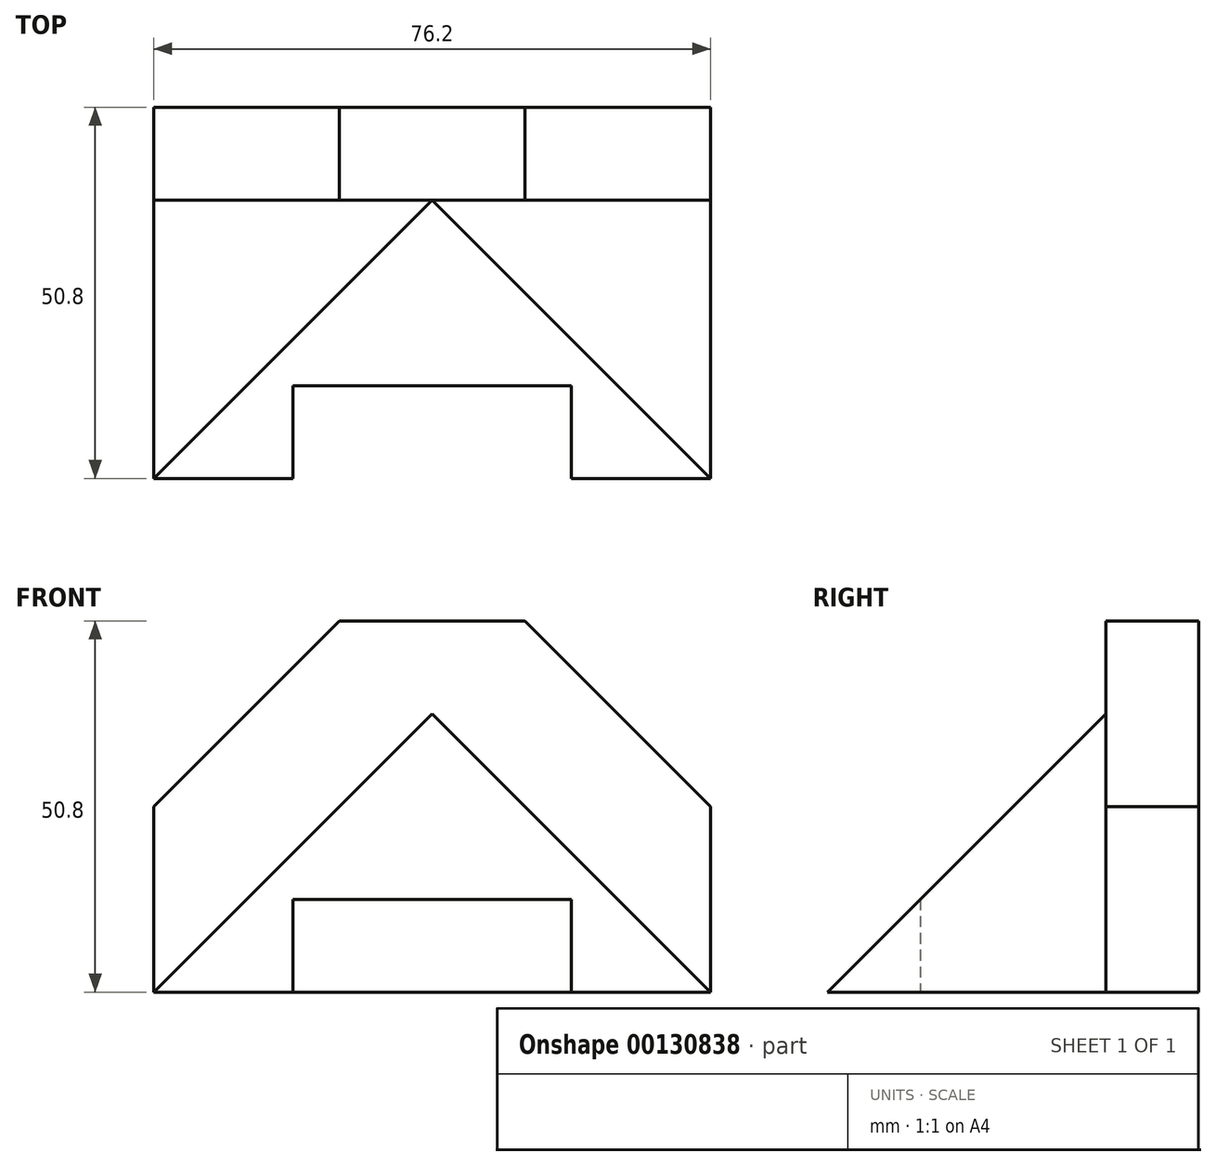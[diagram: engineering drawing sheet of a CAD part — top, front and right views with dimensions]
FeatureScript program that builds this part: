
annotation { "Feature Type Name" : "Feature", "Feature Type Description" : "" }
export const myFeature = defineFeature(function(context is Context, id is Id, definition is map)
    precondition{}
    {
        {
            var Q0;
            Q0=qCreatedBy(makeId("Front.planeOp"),FACE);
            var sketch = newSketch(context, id + "F0", { "sketchPlane" : qUnion([Q0])});
            skLineSegment(sketch, "E0", {"start": v(0, 0) * mm, "end": v(0, 25.4) * mm});
            skLineSegment(sketch, "E1", {"start": v(0, 25.4) * mm, "end": v(25.4, 50.8) * mm});
            skLineSegment(sketch, "E2", {"start": v(25.4, 50.8) * mm, "end": v(50.8, 50.8) * mm});
            skLineSegment(sketch, "E3", {"start": v(50.8, 50.8) * mm, "end": v(76.2, 25.4) * mm});
            skLineSegment(sketch, "E4", {"start": v(76.2, 25.4) * mm, "end": v(76.2, 0) * mm});
            skLineSegment(sketch, "E5", {"start": v(76.2, 0) * mm, "end": v(0, 0) * mm});
            skSolve(sketch);
        }
        {
            var Q0;
            Q0 = qSketchRegion(id + "F0", true);
            extrude(context, id + "F1", {"entities" : qUnion([Q0]), "oppositeDirection" : true, "depth" : 12.7 * mm});
        }
        {
            var Q0;
            Q0=qCreatedBy(makeId("Front.planeOp"),FACE);
            var sketch = newSketch(context, id + "F2", { "sketchPlane" : qUnion([Q0])});
            skLineSegment(sketch, "E6", {"start": v(0, 0) * mm, "end": v(0, 38.1) * mm});
            skLineSegment(sketch, "E7", {"start": v(0, 38.1) * mm, "end": v(76.2, 38.1) * mm});
            skLineSegment(sketch, "E8", {"start": v(76.2, 38.1) * mm, "end": v(76.2, 0) * mm});
            skLineSegment(sketch, "E9", {"start": v(76.2, 0) * mm, "end": v(0, 0) * mm});
            skSolve(sketch);
        }
        {
            var Q0;
            Q0 = qSketchRegion(id + "F2", true);
            extrude(context, id + "F3", {"entities" : qUnion([Q0]), "operationType" : NewBodyOperationType.ADD, "depth" : 38.1 * mm});
        }
        {
            var Q0;
            Q0=makeQuery(id+"F3.opExtrude","CAP_FACE",FACE,{"disambiguationData":[OSD([sQuery(id+"F2.wireOp",EDGE,"E6"),sQuery(id+"F2.wireOp",EDGE,"E7"),sQuery(id+"F2.wireOp",EDGE,"E8"),sQuery(id+"F2.wireOp",EDGE,"E9")])],"isStart":false});
            var sketch = newSketch(context, id + "F4", { "sketchPlane" : qUnion([Q0])});
            skLineSegment(sketch, "E10", {"start": v(0, 0) * mm, "end": v(38.1, 38.1) * mm});
            skLineSegment(sketch, "E11", {"start": v(38.1, 38.1) * mm, "end": v(76.2, 0) * mm});
            skLineSegment(sketch, "E12", {"start": v(0, 0) * mm, "end": v(0, 38.1) * mm});
            skLineSegment(sketch, "E13", {"start": v(0, 38.1) * mm, "end": v(38.1, 38.1) * mm});
            skLineSegment(sketch, "E14", {"start": v(38.1, 38.1) * mm, "end": v(76.2, 38.1) * mm});
            skLineSegment(sketch, "E15", {"start": v(76.2, 38.1) * mm, "end": v(76.2, 0) * mm});
            skSolve(sketch);
        }
        {
            var Q0;
            Q0 = qSketchRegion(id + "F4", true);
            extrude(context, id + "F5", {"entities" : qUnion([Q0]), "operationType" : NewBodyOperationType.REMOVE, "oppositeDirection" : true, "depth" : 38.1 * mm});
        }
        {
            var Q0;
            Q0=qCreatedBy(makeId("Right.planeOp"),FACE);
            var sketch = newSketch(context, id + "F6", { "sketchPlane" : qUnion([Q0])});
            skLineSegment(sketch, "E16.0", {"start": v(0, 38.1) * mm, "end": v(-38.1, 38.1) * mm});
            skLineSegment(sketch, "E17.0", {"start": v(-38.1, 0) * mm, "end": v(-38.1, 38.1) * mm});
            skLineSegment(sketch, "E18", {"start": v(0, 38.1) * mm, "end": v(-38.1, 0) * mm});
            skSolve(sketch);
        }
        {
            var Q0;
            Q0 = qSketchRegion(id + "F6", true);
            extrude(context, id + "F7", {"entities" : qUnion([Q0]), "operationType" : NewBodyOperationType.REMOVE, "endBound" : BoundingType.THROUGH_ALL, "depth" : 25.4 * mm});
        }
        {
            var Q0;
            Q0=qCreatedBy(makeId("Top.planeOp"),FACE);
            var sketch = newSketch(context, id + "F8", { "sketchPlane" : qUnion([Q0])});
            skLineSegment(sketch, "E19.0", {"start": v(57.15, -38.1) * mm, "end": v(19.05, -38.1) * mm});
            skLineSegment(sketch, "E20", {"start": v(19.05, -38.1) * mm, "end": v(19.05, -25.4) * mm});
            skLineSegment(sketch, "E21", {"start": v(19.05, -25.4) * mm, "end": v(57.15, -25.4) * mm});
            skLineSegment(sketch, "E22", {"start": v(57.15, -25.4) * mm, "end": v(57.15, -38.1) * mm});
            skPoint(sketch, "E23.orphan", {"position": v(0, -38.1) * mm});
            skPoint(sketch, "E24.orphan", {"position": v(76.2, -38.1) * mm});
            skSolve(sketch);
        }
        {
            var Q0;
            Q0 = qSketchRegion(id + "F8", true);
            extrude(context, id + "F9", {"entities" : qUnion([Q0]), "operationType" : NewBodyOperationType.REMOVE, "depth" : 25.4 * mm});
        }
    });
